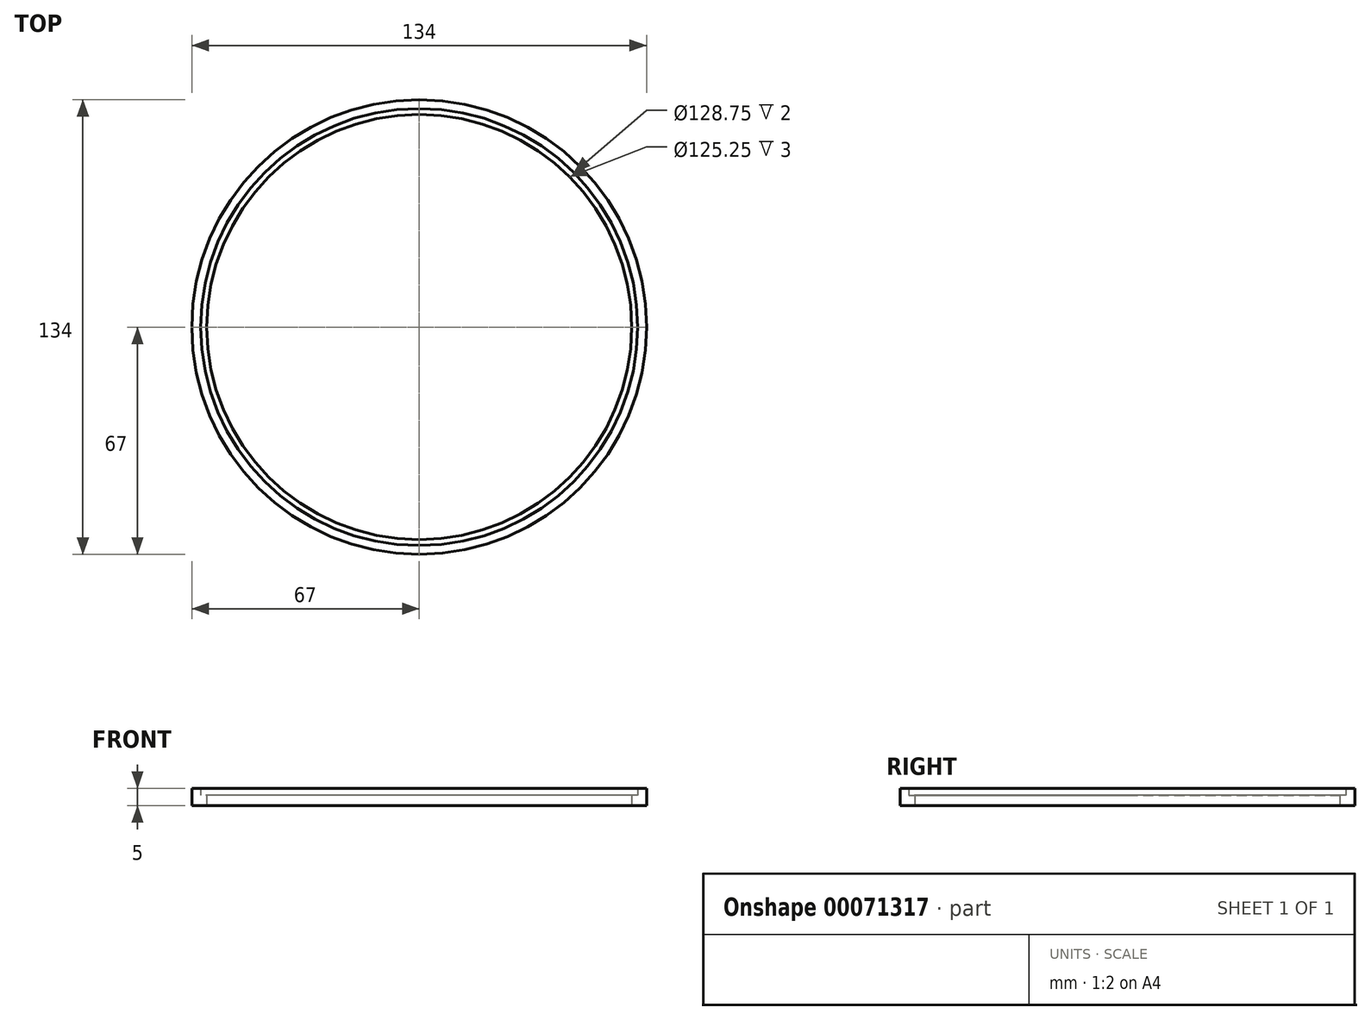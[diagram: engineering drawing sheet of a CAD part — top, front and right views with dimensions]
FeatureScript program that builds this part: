
annotation { "Feature Type Name" : "Feature", "Feature Type Description" : "" }
export const myFeature = defineFeature(function(context is Context, id is Id, definition is map)
    precondition{}
    {
        {
            var Q0;
            Q0=qCreatedBy(makeId("Top.planeOp"),FACE);
            var sketch = newSketch(context, id + "F0", { "sketchPlane" : qUnion([Q0])});
            skCircle(sketch, "E0", {"center": v(0, 0) * mm, "radius": 67 * mm});
            skCircle(sketch, "E1", {"center": v(0, 0) * mm, "radius": 64.38 * mm});
            skCircle(sketch, "E2", {"center": v(0, 0) * mm, "radius": 58.88 * mm});
            skCircle(sketch, "E3", {"center": v(0, 0) * mm, "radius": 62.62 * mm});
            skSolve(sketch);
        }
        {
            var Q0;
            Q0 = qSketchRegion(id + "F0", true);
            var Q1;
            Q1=makeQuery(id+"F0.imprint","IMPRINT",FACE,{"disambiguationData":[TD([[makeQuery(id+"F0.imprint","IMPRINT",EDGE,{"derivedFrom":sQuery(id+"F0.wireOp",EDGE,"E0")}),1.0]])]});
            extrude(context, id + "F1", {"entities" : qUnion([Q0, Q1]), "depth" : 5 * mm});
        }
        {
            var Q0;
            Q0=makeQuery(id+"F0.imprint","IMPRINT",FACE,{"disambiguationData":[TD([[makeQuery(id+"F0.imprint","IMPRINT",EDGE,{"derivedFrom":sQuery(id+"F0.wireOp",EDGE,"E1")}),1.0]])]});
            extrude(context, id + "F2", {"entities" : qUnion([Q0]), "operationType" : NewBodyOperationType.ADD, "depth" : 3 * mm});
        }
        {
            var Q0;
            Q0=makeQuery(id+"F0.imprint","IMPRINT",FACE,{"disambiguationData":[TD([[makeQuery(id+"F0.imprint","IMPRINT",EDGE,{"derivedFrom":sQuery(id+"F0.wireOp",EDGE,"E2")}),-1.0]])]});
            extrude(context, id + "F3", {"entities" : qUnion([Q0]), "operationType" : NewBodyOperationType.REMOVE, "depth" : 2 * mm});
        }
        {
            var Q0;
            Q0=qCreatedBy(makeId("Top.planeOp"),FACE);
            var sketch = newSketch(context, id + "F4", { "sketchPlane" : qUnion([Q0])});
            skCircle(sketch, "E4", {"center": v(0, 0) * mm, "radius": 4.75 * mm});
            skCircle(sketch, "E5", {"center": v(0, 18.75) * mm, "radius": 5.75 * mm});
            skCircle(sketch, "E6", {"center": v(0, 46.25) * mm, "radius": 5.75 * mm});
            skLineSegment(sketch, "E7", {"start": v(0, 0) * mm, "end": v(0, -8) * mm, "construction": true});
            skLineSegment(sketch, "E8", {"start": v(0, -8) * mm, "end": v(17.5, -8) * mm, "construction": true});
            skCircle(sketch, "E9", {"center": v(17.5, -8) * mm, "radius": 2.1 * mm});
            skCircle(sketch, "E10.MirrorC", {"center": v(-17.5, -8) * mm, "radius": 2.1 * mm});
            skSolve(sketch);
        }
        {
            var Q0;
            Q0=makeQuery(id+"F4.imprint","IMPRINT",FACE,{"disambiguationData":[TD([[makeQuery(id+"F4.imprint","IMPRINT",EDGE,{"derivedFrom":sQuery(id+"F4.wireOp",EDGE,"E6")}),1.0]])]});
            extrude(context, id + "F5", {"entities" : qUnion([Q0]), "operationType" : NewBodyOperationType.REMOVE, "endBound" : BoundingType.THROUGH_ALL, "oppositeDirection" : true, "depth" : 74.48 * mm});
        }
    });
